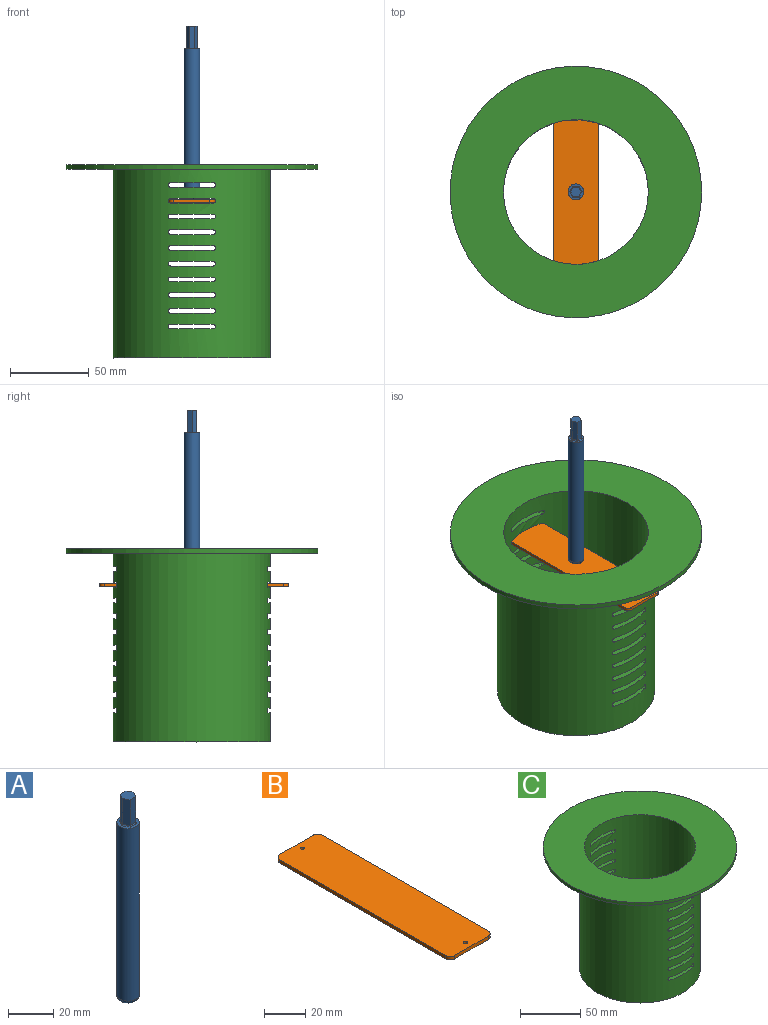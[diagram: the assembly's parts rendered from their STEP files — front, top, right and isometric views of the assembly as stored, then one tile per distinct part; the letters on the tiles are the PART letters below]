
ASSEMBLY  parts=3 mates=2
PART A: 19 faces, bbox 10.8x10.8x110 mm
  f0: cylinder r=5mm len=93.5mm, axis (0,0,-1), area 2937.4mm2, adj f1,f16
  f1: plane 10x10mm, normal (0,0,1), area 36.1mm2, adj f0,f10,f11,f12,f13,f14,f15
  f2: plane 6x6mm, normal (0,0,-1), area 21.2mm2, adj f16,f17
  f3: plane 14x3mm, normal (0.87,0.5,0), area 48.5mm2, adj f4,f8,f9,f12
  f4: plane 14x3.46mm, normal (0,1,0), area 48.5mm2, adj f3,f5,f9,f10
  f5: plane 14x3mm, normal (-0.87,0.5,0), area 48.5mm2, adj f4,f6,f9,f11
  f6: plane 14x3mm, normal (-0.87,-0.5,0), area 48.5mm2, adj f5,f7,f9,f13
  f7: plane 14x3.46mm, normal (0,-1,0), area 48.5mm2, adj f6,f8,f9,f15
  f8: plane 14x3mm, normal (0.87,-0.5,0), area 48.5mm2, adj f3,f7,f9,f14
  f9: plane 6.93x6mm, normal (0,0,1), area 31.2mm2, adj f3,f4,f5,f6,f7,f8
  f10: cylinder r=0.5mm len=4.04mm, axis (-1,0,0), area 2.9mm2, adj f1,f4,f11,f12
  f11: cylinder r=0.5mm len=3.75mm, axis (-0.5,-0.87,0), area 2.9mm2, adj f1,f5,f10,f13
  f12: cylinder r=0.5mm len=3.75mm, axis (-0.5,0.87,0), area 2.9mm2, adj f1,f3,f10,f14
  f13: cylinder r=0.5mm len=3.75mm, axis (0.5,-0.87,0), area 2.9mm2, adj f1,f6,f11,f15
  f14: cylinder r=0.5mm len=3.75mm, axis (0.5,0.87,0), area 2.9mm2, adj f1,f8,f12,f15
  f15: cylinder r=0.5mm len=4.04mm, axis (1,0,0), area 2.9mm2, adj f1,f7,f13,f14
  f16: torus R=3mm, axis (0,0,1), area 84.4mm2, adj f0,f2
  f17: cylinder r=1.5mm len=3mm, axis (0,0,-1), area 18.8mm2, adj f2,f18
  f18: plane 3x3mm, normal (0,0,-1), area 7.1mm2, adj f17
PART B: 12 faces, bbox 29x120x2 mm
  f0: plane 120x29mm, normal (0,0,1), area 3466mm2, adj f2,f3,f4,f5,f6,f7,f8,f9
  f1: plane 120x29mm, normal (0,0,-1), area 3466mm2, adj f2,f3,f4,f5,f6,f7,f8,f9
  f2: plane 23x2mm, normal (0,1,0), area 46mm2, adj f0,f1,f6,f9
  f3: plane 114x2mm, normal (-1,0,0), area 228mm2, adj f0,f1,f6,f7
  f4: plane 23x2mm, normal (0,-1,0), area 46mm2, adj f0,f1,f7,f8
  f5: plane 114x2mm, normal (1,0,0), area 228mm2, adj f0,f1,f8,f9
  f6: cylinder r=3mm len=3mm, axis (0,0,-1), area 9.4mm2, adj f0,f1,f2,f3
  f7: cylinder r=3mm len=3mm, axis (0,0,-1), area 9.4mm2, adj f0,f1,f3,f4
  f8: cylinder r=3mm len=3mm, axis (0,0,-1), area 9.4mm2, adj f0,f1,f4,f5
  f9: cylinder r=3mm len=3mm, axis (0,0,-1), area 9.4mm2, adj f0,f1,f2,f5
  f10: cylinder r=1mm len=2mm, axis (0,0,1), area 12.6mm2, adj f0,f1
  f11: cylinder r=1mm len=2mm, axis (0,0,1), area 12.6mm2, adj f0,f1
PART C: 86 faces, bbox 160x160x123 mm
  f0: cylinder r=50mm len=120mm, axis (0,0,-1), area 35911.3mm2, adj f2,f3,f6,f7,f8,f9,f10,f11
  f1: cylinder r=46mm len=123mm, axis (0,0,1), area 33757.2mm2, adj f2,f4,f6,f7,f8,f9,f10,f11
  f2: plane 100x100mm, normal (0,0,-1), area 1206.4mm2, adj f0,f1
  f3: plane 160x160mm, normal (0,0,-1), area 12252.2mm2, adj f0,f5
  f4: plane 160x160mm, normal (0,0,1), area 13458.6mm2, adj f1,f5
  f5: cylinder r=80mm len=160mm, axis (0,0,-1), area 1508mm2, adj f3,f4
  f6: plane 27x6.03mm, normal (0,0,1), area 109.5mm2, adj f0,f1,f7,f9
  f7: cylinder r=1.5mm len=4.66mm, axis (0,-1,0), area 19.8mm2, adj f0,f1,f6,f8
  f8: plane 27x6.03mm, normal (0,0,-1), area 109.5mm2, adj f0,f1,f7,f9
  f9: cylinder r=1.5mm len=4.66mm, axis (0,-1,0), area 19.8mm2, adj f0,f1,f6,f8
  f10: cylinder r=1.5mm len=4.66mm, axis (0,-1,0), area 19.8mm2, adj f0,f1,f11,f13
  f11: plane 27x6.03mm, normal (0,0,-1), area 109.5mm2, adj f0,f1,f10,f12
  f12: cylinder r=1.5mm len=4.66mm, axis (0,-1,0), area 19.8mm2, adj f0,f1,f11,f13
  f13: plane 27x6.03mm, normal (0,0,1), area 109.5mm2, adj f0,f1,f10,f12
  f14: cylinder r=1.5mm len=4.66mm, axis (0,-1,0), area 19.8mm2, adj f0,f1,f15,f17
  f15: plane 27x6.03mm, normal (0,0,-1), area 109.5mm2, adj f0,f1,f14,f16
  f16: cylinder r=1.5mm len=4.66mm, axis (0,-1,0), area 19.8mm2, adj f0,f1,f15,f17
  f17: plane 27x6.03mm, normal (0,0,1), area 109.5mm2, adj f0,f1,f14,f16
  f18: plane 27x6.03mm, normal (0,0,1), area 109.5mm2, adj f0,f1,f19,f21
  f19: cylinder r=1.5mm len=4.66mm, axis (0,-1,0), area 19.8mm2, adj f0,f1,f18,f20
  f20: plane 27x6.03mm, normal (0,0,-1), area 109.5mm2, adj f0,f1,f19,f21
  f21: cylinder r=1.5mm len=4.66mm, axis (0,-1,0), area 19.8mm2, adj f0,f1,f18,f20
  f22: cylinder r=1.5mm len=4.66mm, axis (0,-1,0), area 19.8mm2, adj f0,f1,f23,f25
  f23: plane 27x6.03mm, normal (0,0,-1), area 109.5mm2, adj f0,f1,f22,f24
  f24: cylinder r=1.5mm len=4.66mm, axis (0,-1,0), area 19.8mm2, adj f0,f1,f23,f25
  f25: plane 27x6.03mm, normal (0,0,1), area 109.5mm2, adj f0,f1,f22,f24
  f26: plane 27x6.03mm, normal (0,0,1), area 109.5mm2, adj f0,f1,f27,f29
  f27: cylinder r=1.5mm len=4.66mm, axis (0,-1,0), area 19.8mm2, adj f0,f1,f26,f28
  f28: plane 27x6.03mm, normal (0,0,-1), area 109.5mm2, adj f0,f1,f27,f29
  f29: cylinder r=1.5mm len=4.66mm, axis (0,-1,0), area 19.8mm2, adj f0,f1,f26,f28
  f30: cylinder r=1.5mm len=4.66mm, axis (0,-1,0), area 19.8mm2, adj f0,f1,f31,f33
  f31: plane 27x6.03mm, normal (0,0,-1), area 109.5mm2, adj f0,f1,f30,f32
  f32: cylinder r=1.5mm len=4.66mm, axis (0,-1,0), area 19.8mm2, adj f0,f1,f31,f33
  f33: plane 27x6.03mm, normal (0,0,1), area 109.5mm2, adj f0,f1,f30,f32
  f34: plane 27x6.03mm, normal (0,0,1), area 109.5mm2, adj f0,f1,f35,f37
  f35: cylinder r=1.5mm len=4.66mm, axis (0,-1,0), area 19.8mm2, adj f0,f1,f34,f36
  f36: plane 27x6.03mm, normal (0,0,-1), area 109.5mm2, adj f0,f1,f35,f37
  f37: cylinder r=1.5mm len=4.66mm, axis (0,-1,0), area 19.8mm2, adj f0,f1,f34,f36
  f38: cylinder r=1.5mm len=4.66mm, axis (0,-1,0), area 19.8mm2, adj f0,f1,f39,f41
  f39: plane 27x6.03mm, normal (0,0,-1), area 109.5mm2, adj f0,f1,f38,f40
  f40: cylinder r=1.5mm len=4.66mm, axis (0,-1,0), area 19.8mm2, adj f0,f1,f39,f41
  f41: plane 27x6.03mm, normal (0,0,1), area 109.5mm2, adj f0,f1,f38,f40
  f42: plane 27x6.03mm, normal (0,0,1), area 109.5mm2, adj f0,f1,f43,f45
  f43: cylinder r=1.5mm len=4.66mm, axis (0,-1,0), area 19.8mm2, adj f0,f1,f42,f44
  f44: plane 27x6.03mm, normal (0,0,-1), area 109.5mm2, adj f0,f1,f43,f45
  f45: cylinder r=1.5mm len=4.66mm, axis (0,-1,0), area 19.8mm2, adj f0,f1,f42,f44
  f46: cylinder r=1.5mm len=4.66mm, axis (0,-1,0), area 19.8mm2, adj f0,f1,f47,f49
  f47: plane 27x6.03mm, normal (0,0,-1), area 109.5mm2, adj f0,f1,f46,f48
  f48: cylinder r=1.5mm len=4.66mm, axis (0,-1,0), area 19.8mm2, adj f0,f1,f47,f49
  f49: plane 27x6.03mm, normal (0,0,1), area 109.5mm2, adj f0,f1,f46,f48
  f50: plane 27x6.03mm, normal (0,0,1), area 109.5mm2, adj f0,f1,f51,f53
  f51: cylinder r=1.5mm len=4.66mm, axis (0,-1,0), area 19.8mm2, adj f0,f1,f50,f52
  f52: plane 27x6.03mm, normal (0,0,-1), area 109.5mm2, adj f0,f1,f51,f53
  f53: cylinder r=1.5mm len=4.66mm, axis (0,-1,0), area 19.8mm2, adj f0,f1,f50,f52
  f54: cylinder r=1.5mm len=4.66mm, axis (0,-1,0), area 19.8mm2, adj f0,f1,f55,f57
  f55: plane 27x6.03mm, normal (0,0,-1), area 109.5mm2, adj f0,f1,f54,f56
  f56: cylinder r=1.5mm len=4.66mm, axis (0,-1,0), area 19.8mm2, adj f0,f1,f55,f57
  f57: plane 27x6.03mm, normal (0,0,1), area 109.5mm2, adj f0,f1,f54,f56
  f58: plane 27x6.03mm, normal (0,0,1), area 109.5mm2, adj f0,f1,f59,f61
  f59: cylinder r=1.5mm len=4.66mm, axis (0,-1,0), area 19.8mm2, adj f0,f1,f58,f60
  f60: plane 27x6.03mm, normal (0,0,-1), area 109.5mm2, adj f0,f1,f59,f61
  f61: cylinder r=1.5mm len=4.66mm, axis (0,-1,0), area 19.8mm2, adj f0,f1,f58,f60
  f62: cylinder r=1.5mm len=4.66mm, axis (0,-1,0), area 19.8mm2, adj f0,f1,f63,f65
  f63: plane 27x6.03mm, normal (0,0,-1), area 109.5mm2, adj f0,f1,f62,f64
  f64: cylinder r=1.5mm len=4.66mm, axis (0,-1,0), area 19.8mm2, adj f0,f1,f63,f65
  f65: plane 27x6.03mm, normal (0,0,1), area 109.5mm2, adj f0,f1,f62,f64
  f66: plane 27x6.03mm, normal (0,0,1), area 109.5mm2, adj f0,f1,f67,f69
  f67: cylinder r=1.5mm len=4.66mm, axis (0,-1,0), area 19.8mm2, adj f0,f1,f66,f68
  f68: plane 27x6.03mm, normal (0,0,-1), area 109.5mm2, adj f0,f1,f67,f69
  f69: cylinder r=1.5mm len=4.66mm, axis (0,-1,0), area 19.8mm2, adj f0,f1,f66,f68
  f70: cylinder r=1.5mm len=4.66mm, axis (0,-1,0), area 19.8mm2, adj f0,f1,f71,f73
  f71: plane 27x6.03mm, normal (0,0,-1), area 109.5mm2, adj f0,f1,f70,f72
  f72: cylinder r=1.5mm len=4.66mm, axis (0,-1,0), area 19.8mm2, adj f0,f1,f71,f73
  f73: plane 27x6.03mm, normal (0,0,1), area 109.5mm2, adj f0,f1,f70,f72
  f74: plane 27x6.03mm, normal (0,0,1), area 109.5mm2, adj f0,f1,f75,f77
  f75: cylinder r=1.5mm len=4.66mm, axis (0,-1,0), area 19.8mm2, adj f0,f1,f74,f76
  f76: plane 27x6.03mm, normal (0,0,-1), area 109.5mm2, adj f0,f1,f75,f77
  f77: cylinder r=1.5mm len=4.66mm, axis (0,-1,0), area 19.8mm2, adj f0,f1,f74,f76
  f78: cylinder r=1.5mm len=4.66mm, axis (0,-1,0), area 19.8mm2, adj f0,f1,f79,f81
  f79: plane 27x6.03mm, normal (0,0,1), area 109.5mm2, adj f0,f1,f78,f80
  f80: cylinder r=1.5mm len=4.66mm, axis (0,-1,0), area 19.8mm2, adj f0,f1,f79,f81
  f81: plane 27x6.03mm, normal (0,0,-1), area 109.5mm2, adj f0,f1,f78,f80
  f82: plane 27x6.03mm, normal (0,0,-1), area 109.5mm2, adj f0,f1,f83,f85
  f83: cylinder r=1.5mm len=4.66mm, axis (0,-1,0), area 19.8mm2, adj f0,f1,f82,f84
  f84: plane 27x6.03mm, normal (0,0,1), area 109.5mm2, adj f0,f1,f83,f85
  f85: cylinder r=1.5mm len=4.66mm, axis (0,-1,0), area 19.8mm2, adj f0,f1,f82,f84
PLACE A t=(-80.48,-286.4,130.34)mm
PLACE B t=(-94.98,-272.17,128.2)mm
PLACE C rot(axis=(0.01,-1,0.04),0deg) t=(-80.48,-286.4,29.2)mm
MATE slider A.f0 <-> C.f1  axis (0,0,-1) through (-80.48,-286.4,132.34)mm
MATE slider C.f17 <-> B.f1  axis (0,0,1) through (-80.48,-333.76,127.7)mm
